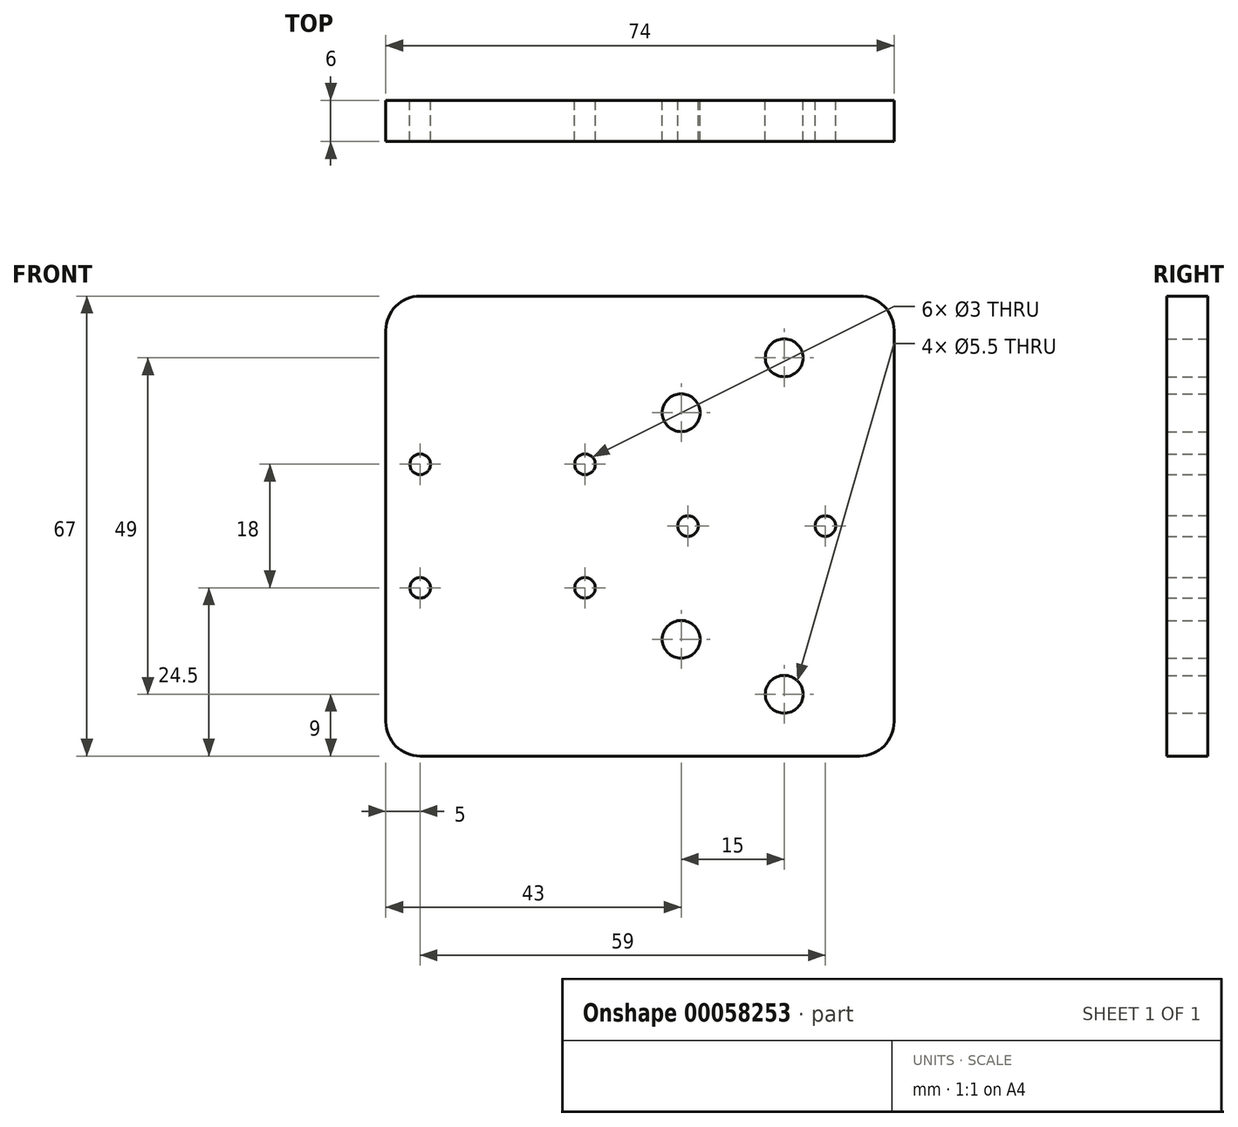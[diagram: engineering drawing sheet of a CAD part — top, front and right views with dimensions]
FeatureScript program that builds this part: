
annotation { "Feature Type Name" : "Feature", "Feature Type Description" : "" }
export const myFeature = defineFeature(function(context is Context, id is Id, definition is map)
    precondition{}
    {
        {
            var Q0;
            Q0=qCreatedBy(makeId("Front.planeOp"),FACE);
            var sketch = newSketch(context, id + "F0", { "sketchPlane" : qUnion([Q0])});
            skLineSegment(sketch, "E0.bottom", {"start": v(12, 9) * mm, "end": v(-12, 9) * mm, "construction": true});
            skLineSegment(sketch, "E0.top", {"start": v(12, -9) * mm, "end": v(-12, -9) * mm, "construction": true});
            skLineSegment(sketch, "E0.left", {"start": v(12, 9) * mm, "end": v(12, -9) * mm, "construction": true});
            skLineSegment(sketch, "E0.right", {"start": v(-12, 9) * mm, "end": v(-12, -9) * mm, "construction": true});
            skPoint(sketch, "E0.middle", {"position": v(0, 0) * mm});
            skCircle(sketch, "E1", {"center": v(-12, 9) * mm, "radius": 1.5 * mm});
            skCircle(sketch, "E2", {"center": v(12, 9) * mm, "radius": 1.5 * mm});
            skCircle(sketch, "E3", {"center": v(-12, -9) * mm, "radius": 1.5 * mm});
            skCircle(sketch, "E4", {"center": v(12, -9) * mm, "radius": 1.5 * mm});
            skLineSegment(sketch, "E5.bottom", {"start": v(17, 15) * mm, "end": v(-17, 15) * mm, "construction": true});
            skLineSegment(sketch, "E5.top", {"start": v(17, -15) * mm, "end": v(-17, -15) * mm, "construction": true});
            skLineSegment(sketch, "E5.left", {"start": v(17, 15) * mm, "end": v(17, -15) * mm, "construction": true});
            skLineSegment(sketch, "E5.right", {"start": v(-17, 15) * mm, "end": v(-17, -15) * mm, "construction": true});
            skLineSegment(sketch, "E6", {"start": v(0, 0) * mm, "end": v(69.39, 0) * mm, "construction": true});
            skCircle(sketch, "E7", {"center": v(26, 16.5) * mm, "radius": 8 * mm, "construction": true});
            skCircle(sketch, "E8", {"center": v(41, 24.5) * mm, "radius": 8 * mm, "construction": true});
            skPoint(sketch, "E9", {"position": v(34, 16.5) * mm});
            skPoint(sketch, "E10", {"position": v(33, 24.5) * mm});
            skPoint(sketch, "E11", {"position": v(18, 16.5) * mm});
            skCircle(sketch, "E12", {"center": v(26, 16.5) * mm, "radius": 2.75 * mm});
            skCircle(sketch, "E13", {"center": v(41, 24.5) * mm, "radius": 2.75 * mm});
            skCircle(sketch, "E14", {"center": v(26, 16.5) * mm, "radius": 7.5 * mm, "construction": true});
            skCircle(sketch, "E15", {"center": v(41, 24.5) * mm, "radius": 7.5 * mm, "construction": true});
            skLineSegment(sketch, "E16", {"start": v(26, 16.5) * mm, "end": v(33.5, 16.5) * mm, "construction": true});
            skLineSegment(sketch, "E17", {"start": v(33.5, 16.5) * mm, "end": v(33.5, 24.5) * mm, "construction": true});
            skLineSegment(sketch, "E18", {"start": v(0, 0) * mm, "end": v(0, 7.5) * mm, "construction": true});
            skLineSegment(sketch, "E19", {"start": v(0, 7.5) * mm, "end": v(65.82, 7.5) * mm, "construction": true});
            skPoint(sketch, "E20", {"position": v(26, 8.5) * mm});
            skCircle(sketch, "E21.MirrorC", {"center": v(41, -24.5) * mm, "radius": 2.75 * mm});
            skCircle(sketch, "E22.MirrorC", {"center": v(26, -16.5) * mm, "radius": 2.75 * mm});
            skLineSegment(sketch, "E23", {"start": v(-17, 33.5) * mm, "end": v(57, 33.5) * mm});
            skCircle(sketch, "E24", {"center": v(27, 0) * mm, "radius": 1.5 * mm});
            skCircle(sketch, "E25", {"center": v(47, 0) * mm, "radius": 1.5 * mm});
            skLineSegment(sketch, "E26.MirrorCS", {"start": v(-17, -33.5) * mm, "end": v(57, -33.5) * mm});
            skLineSegment(sketch, "E27", {"start": v(-17, 33.5) * mm, "end": v(-17, -33.5) * mm});
            skLineSegment(sketch, "E28", {"start": v(57, 33.5) * mm, "end": v(57, -33.5) * mm});
            skSolve(sketch);
        }
        {
            var Q0;
            Q0 = qSketchRegion(id + "F0", true);
            extrude(context, id + "F1", {"entities" : qUnion([Q0]), "depth" : 6 * mm});
        }
        {
            var Q0;
            Q0=makeQuery(id+"F1.opExtrude","SWEPT_EDGE",EDGE,{"disambiguationData":[OSD([sQuery(id+"F0.wireOp",EDGE,"E23"),sQuery(id+"F0.wireOp",EDGE,"E27")])]});
            var Q1;
            Q1=makeQuery(id+"F1.opExtrude","SWEPT_EDGE",EDGE,{"disambiguationData":[OSD([sQuery(id+"F0.wireOp",EDGE,"E23"),sQuery(id+"F0.wireOp",EDGE,"E28")])]});
            var Q2;
            Q2=makeQuery(id+"F1.opExtrude","SWEPT_EDGE",EDGE,{"disambiguationData":[OSD([sQuery(id+"F0.wireOp",EDGE,"E26.MirrorCS"),sQuery(id+"F0.wireOp",EDGE,"E28")])]});
            var Q3;
            Q3=makeQuery(id+"F1.opExtrude","SWEPT_EDGE",EDGE,{"disambiguationData":[OSD([sQuery(id+"F0.wireOp",EDGE,"E26.MirrorCS"),sQuery(id+"F0.wireOp",EDGE,"E27")])]});
            fillet(context, id + "F2", {"entities" : qUnion([Q0, Q1, Q2, Q3]), "radius" : 5 * mm, "tangentPropagation" : true, "allowEdgeOverflow" : false});
        }
    });
